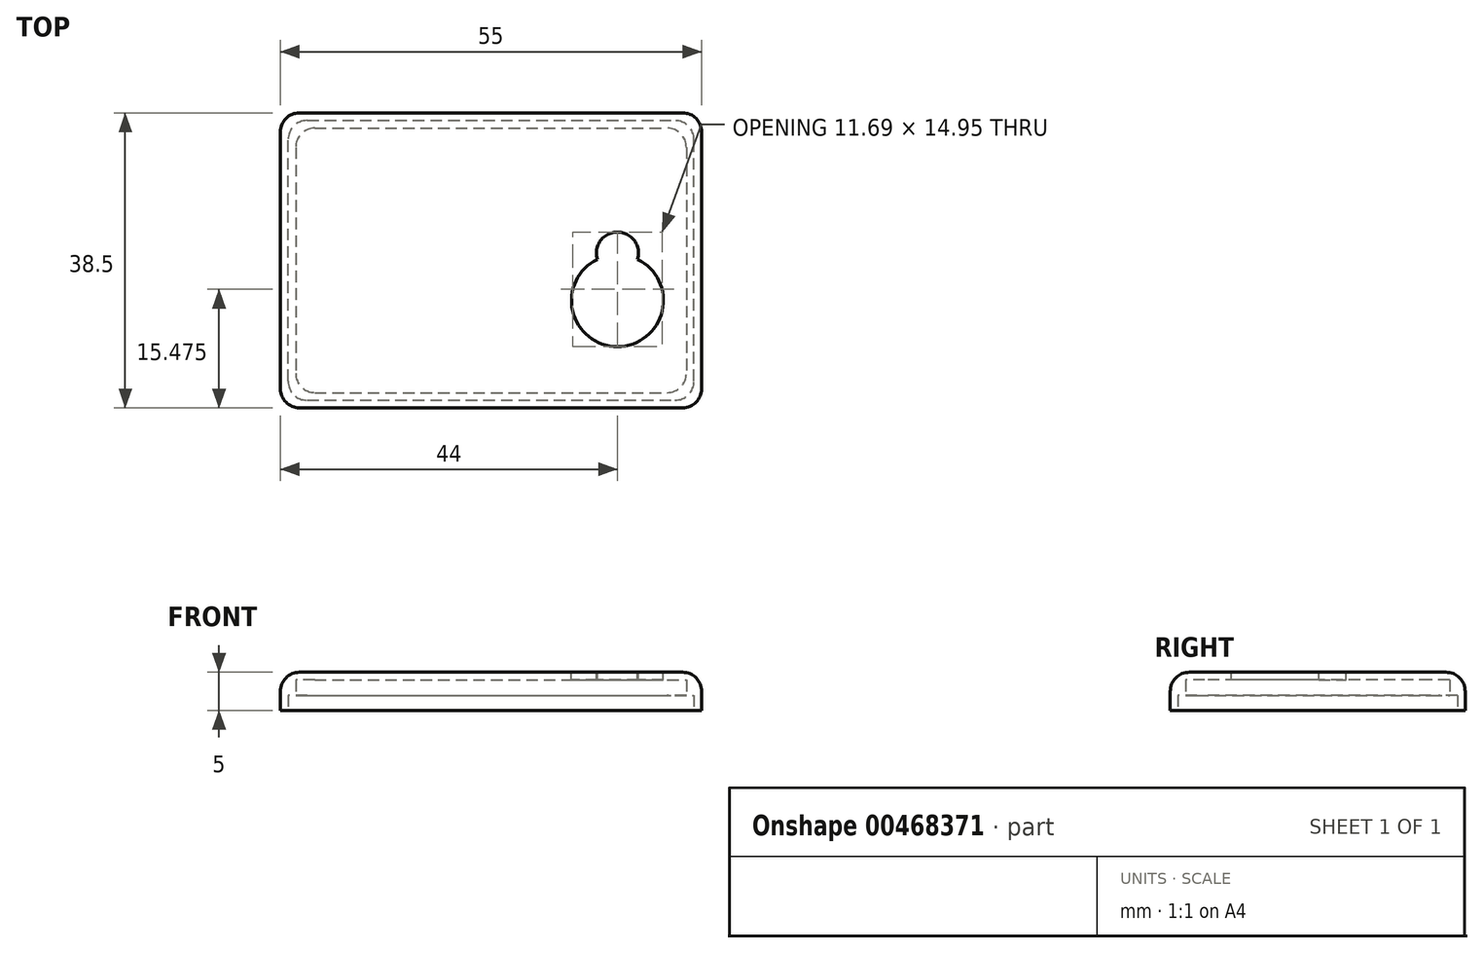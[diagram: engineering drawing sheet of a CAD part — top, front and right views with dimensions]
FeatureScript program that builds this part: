
annotation { "Feature Type Name" : "Feature", "Feature Type Description" : "" }
export const myFeature = defineFeature(function(context is Context, id is Id, definition is map)
    precondition{}
    {
        {
            var Q0;
            Q0=qCreatedBy(makeId("Top.planeOp"),FACE);
            var sketch = newSketch(context, id + "F0", { "sketchPlane" : qUnion([Q0])});
            skLineSegment(sketch, "E0.bottom", {"start": v(27.5, 19.25) * mm, "end": v(-27.5, 19.25) * mm});
            skLineSegment(sketch, "E0.top", {"start": v(27.5, -19.25) * mm, "end": v(-27.5, -19.25) * mm});
            skLineSegment(sketch, "E0.left", {"start": v(27.5, 19.25) * mm, "end": v(27.5, -19.25) * mm});
            skLineSegment(sketch, "E0.right", {"start": v(-27.5, 19.25) * mm, "end": v(-27.5, -19.25) * mm});
            skPoint(sketch, "E0.middle", {"position": v(0, 0) * mm});
            skPoint(sketch, "E1", {"position": v(16.5, -5.25) * mm});
            skCircle(sketch, "E2", {"center": v(16.5, -5.25) * mm, "radius": 6 * mm});
            skCircle(sketch, "E3", {"center": v(16.5, 0.95) * mm, "radius": 2.75 * mm});
            skLineSegment(sketch, "E4", {"start": v(10.5, 0.95) * mm, "end": v(10.5, -5.25) * mm});
            skLineSegment(sketch, "E5", {"start": v(22.5, 0.95) * mm, "end": v(22.5, -5.25) * mm});
            skSolve(sketch);
        }
        {
            var Q0;
            Q0=makeQuery(id+"F0.imprint","IMPRINT",FACE,{"disambiguationData":[TD([[makeQuery(id+"F0.imprint","IMPRINT",EDGE,{"derivedFrom":sQuery(id+"F0.wireOp",EDGE,"E0.bottom")}),1.0]])]});
            extrude(context, id + "F1", {"entities" : qUnion([Q0]), "oppositeDirection" : true, "depth" : 5 * mm});
        }
        {
            var Q0;
            Q0=makeQuery(id+"F1.opExtrude","CAP_FACE",FACE,{"disambiguationData":[OSD([sQuery(id+"F0.wireOp",EDGE,"E0.bottom"),sQuery(id+"F0.wireOp",EDGE,"E0.top"),sQuery(id+"F0.wireOp",EDGE,"E0.left"),sQuery(id+"F0.wireOp",EDGE,"E0.right")])],"isStart":false});
            var sketch = newSketch(context, id + "F2", { "sketchPlane" : qUnion([Q0])});
            skLineSegment(sketch, "E6.bottom", {"start": v(-26.5, 18.25) * mm, "end": v(26.5, 18.25) * mm});
            skLineSegment(sketch, "E6.top", {"start": v(-26.5, -18.25) * mm, "end": v(26.5, -18.25) * mm});
            skLineSegment(sketch, "E6.left", {"start": v(-26.5, 18.25) * mm, "end": v(-26.5, -18.25) * mm});
            skLineSegment(sketch, "E6.right", {"start": v(26.5, 18.25) * mm, "end": v(26.5, -18.25) * mm});
            skPoint(sketch, "E6.middle", {"position": v(0, 0) * mm});
            skLineSegment(sketch, "E7.bottom", {"start": v(-25.5, -17.25) * mm, "end": v(25.5, -17.25) * mm});
            skLineSegment(sketch, "E7.top", {"start": v(-25.5, 17.25) * mm, "end": v(25.5, 17.25) * mm});
            skLineSegment(sketch, "E7.left", {"start": v(-25.5, -17.25) * mm, "end": v(-25.5, 17.25) * mm});
            skLineSegment(sketch, "E7.right", {"start": v(25.5, -17.25) * mm, "end": v(25.5, 17.25) * mm});
            skSolve(sketch);
        }
        {
            var Q0;
            Q0=makeQuery(id+"F2.imprint","IMPRINT",FACE,{"disambiguationData":[TD([[makeQuery(id+"F2.imprint","IMPRINT",EDGE,{"derivedFrom":sQuery(id+"F2.wireOp",EDGE,"E7.bottom")}),1.0]])]});
            extrude(context, id + "F3", {"entities" : qUnion([Q0]), "operationType" : NewBodyOperationType.REMOVE, "oppositeDirection" : true, "depth" : 4 * mm});
        }
        {
            var Q0;
            Q0=makeQuery(id+"F2.imprint","IMPRINT",FACE,{"disambiguationData":[TD([[makeQuery(id+"F2.imprint","IMPRINT",EDGE,{"derivedFrom":sQuery(id+"F2.wireOp",EDGE,"E6.bottom")}),-1.0]])]});
            extrude(context, id + "F4", {"entities" : qUnion([Q0]), "operationType" : NewBodyOperationType.REMOVE, "oppositeDirection" : true, "depth" : 2 * mm});
        }
        {
            var Q0;
            Q0=makeQuery(id+"F1.opExtrude","SWEPT_EDGE",EDGE,{"disambiguationData":[OSD([sQuery(id+"F0.wireOp",EDGE,"E0.bottom"),sQuery(id+"F0.wireOp",EDGE,"E0.right")])]});
            var Q1;
            Q1=makeQuery(id+"F4.boolean.opBoolean","COPY",EDGE,{"derivedFrom":makeQuery(id+"F4.opExtrude","SWEPT_EDGE",EDGE,{"disambiguationData":[OSD([sQuery(id+"F2.wireOp",EDGE,"E6.top"),sQuery(id+"F2.wireOp",EDGE,"E6.left")])]})});
            var Q2;
            Q2=makeQuery(id+"F3.boolean.opBoolean","COPY",EDGE,{"derivedFrom":makeQuery(id+"F3.opExtrude","SWEPT_EDGE",EDGE,{"disambiguationData":[OSD([sQuery(id+"F2.wireOp",EDGE,"E7.bottom"),sQuery(id+"F2.wireOp",EDGE,"E7.left")])]})});
            var Q3;
            Q3=makeQuery(id+"F1.opExtrude","SWEPT_EDGE",EDGE,{"disambiguationData":[OSD([sQuery(id+"F0.wireOp",EDGE,"E0.top"),sQuery(id+"F0.wireOp",EDGE,"E0.right")])]});
            var Q4;
            Q4=makeQuery(id+"F4.boolean.opBoolean","COPY",EDGE,{"derivedFrom":makeQuery(id+"F4.opExtrude","SWEPT_EDGE",EDGE,{"disambiguationData":[OSD([sQuery(id+"F2.wireOp",EDGE,"E6.bottom"),sQuery(id+"F2.wireOp",EDGE,"E6.left")])]})});
            var Q5;
            Q5=makeQuery(id+"F3.boolean.opBoolean","COPY",EDGE,{"derivedFrom":makeQuery(id+"F3.opExtrude","SWEPT_EDGE",EDGE,{"disambiguationData":[OSD([sQuery(id+"F2.wireOp",EDGE,"E7.top"),sQuery(id+"F2.wireOp",EDGE,"E7.left")])]})});
            var Q6;
            Q6=makeQuery(id+"F1.opExtrude","SWEPT_EDGE",EDGE,{"disambiguationData":[OSD([sQuery(id+"F0.wireOp",EDGE,"E0.top"),sQuery(id+"F0.wireOp",EDGE,"E0.left")])]});
            var Q7;
            Q7=makeQuery(id+"F1.opExtrude","SWEPT_EDGE",EDGE,{"disambiguationData":[OSD([sQuery(id+"F0.wireOp",EDGE,"E0.bottom"),sQuery(id+"F0.wireOp",EDGE,"E0.left")])]});
            var Q8;
            Q8=makeQuery(id+"F4.boolean.opBoolean","COPY",EDGE,{"derivedFrom":makeQuery(id+"F4.opExtrude","SWEPT_EDGE",EDGE,{"disambiguationData":[OSD([sQuery(id+"F2.wireOp",EDGE,"E6.bottom"),sQuery(id+"F2.wireOp",EDGE,"E6.right")])]})});
            var Q9;
            Q9=makeQuery(id+"F3.boolean.opBoolean","COPY",EDGE,{"derivedFrom":makeQuery(id+"F3.opExtrude","SWEPT_EDGE",EDGE,{"disambiguationData":[OSD([sQuery(id+"F2.wireOp",EDGE,"E7.top"),sQuery(id+"F2.wireOp",EDGE,"E7.right")])]})});
            var Q10;
            Q10=makeQuery(id+"F4.boolean.opBoolean","COPY",EDGE,{"derivedFrom":makeQuery(id+"F4.opExtrude","SWEPT_EDGE",EDGE,{"disambiguationData":[OSD([sQuery(id+"F2.wireOp",EDGE,"E6.top"),sQuery(id+"F2.wireOp",EDGE,"E6.right")])]})});
            var Q11;
            Q11=makeQuery(id+"F3.boolean.opBoolean","COPY",EDGE,{"derivedFrom":makeQuery(id+"F3.opExtrude","SWEPT_EDGE",EDGE,{"disambiguationData":[OSD([sQuery(id+"F2.wireOp",EDGE,"E7.bottom"),sQuery(id+"F2.wireOp",EDGE,"E7.right")])]})});
            fillet(context, id + "F5", {"entities" : qUnion([Q0, Q1, Q2, Q3, Q4, Q5, Q6, Q7, Q8, Q9, Q10, Q11]), "radius" : 2.5 * mm, "tangentPropagation" : true, "allowEdgeOverflow" : false});
        }
        {
            var Q0;
            Q0=makeQuery(id+"F1.opExtrude","CAP_EDGE",EDGE,{"disambiguationData":[OSD([sQuery(id+"F0.wireOp",EDGE,"E0.right")])],"isStart":true});
            fillet(context, id + "F6", {"entities" : qUnion([Q0]), "radius" : 2.5 * mm, "tangentPropagation" : true, "allowEdgeOverflow" : false});
        }
    });
